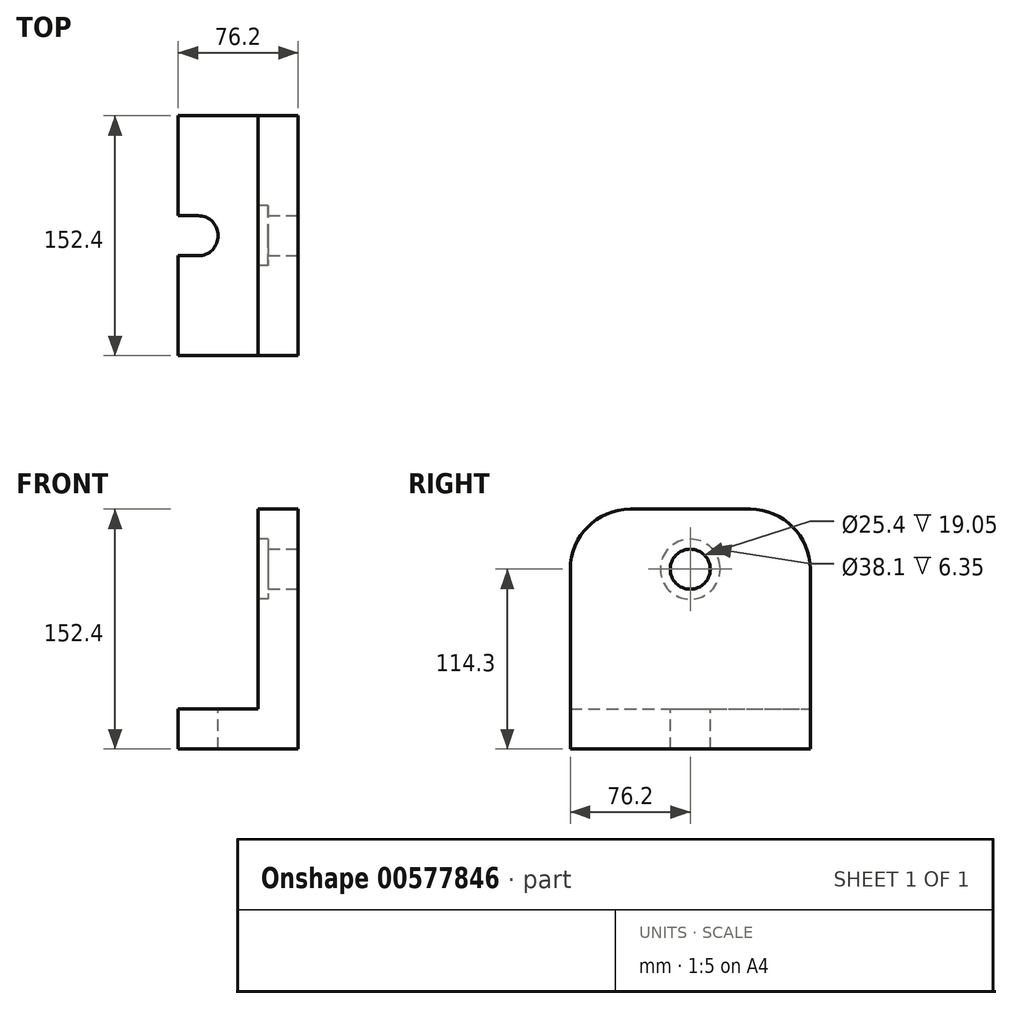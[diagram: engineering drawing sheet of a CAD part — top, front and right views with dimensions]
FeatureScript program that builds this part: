
annotation { "Feature Type Name" : "Feature", "Feature Type Description" : "" }
export const myFeature = defineFeature(function(context is Context, id is Id, definition is map)
    precondition{}
    {
        {
            var Q0;
            Q0=qCreatedBy(makeId("Front.planeOp"),FACE);
            var sketch = newSketch(context, id + "F0", { "sketchPlane" : qUnion([Q0])});
            skLineSegment(sketch, "E0.bottom", {"start": v(0, 0) * mm, "end": v(-76.2, 0) * mm});
            skLineSegment(sketch, "E0.top", {"start": v(-25.4, 25.4) * mm, "end": v(-76.2, 25.4) * mm});
            skLineSegment(sketch, "E0.left", {"start": v(0, 0) * mm, "end": v(0, 25.4) * mm});
            skLineSegment(sketch, "E0.right", {"start": v(-76.2, 0) * mm, "end": v(-76.2, 25.4) * mm});
            skLineSegment(sketch, "E1.bottom", {"start": v(0, 0) * mm, "end": v(-25.4, 0) * mm});
            skLineSegment(sketch, "E1.top", {"start": v(0, 152.4) * mm, "end": v(-25.4, 152.4) * mm});
            skLineSegment(sketch, "E1.left", {"start": v(0, 0) * mm, "end": v(0, 152.4) * mm});
            skLineSegment(sketch, "E1.right", {"start": v(-25.4, 25.4) * mm, "end": v(-25.4, 152.4) * mm});
            skSolve(sketch);
        }
        {
            var Q0;
            Q0=makeQuery(id+"F0.imprint","IMPRINT",FACE,{"disambiguationData":[TD([[makeQuery(id+"F0.imprint","IMPRINT",EDGE,{"derivedFrom":sQuery(id+"F0.wireOp",EDGE,"E0.bottom")}),-1.0]])]});
            extrude(context, id + "F1", {"entities" : qUnion([Q0]), "endBound" : BoundingType.SYMMETRIC, "depth" : 152.4 * mm, "offsetDistance" : 25.4 * mm});
        }
        {
            var Q0;
            Q0=makeQuery(id+"F1.opExtrude","SWEPT_FACE",FACE,{"disambiguationData":[OSD([sQuery(id+"F0.wireOp",EDGE,"E1.left")])]});
            var sketch = newSketch(context, id + "F2", { "sketchPlane" : qUnion([Q0])});
            skCircle(sketch, "E2", {"center": v(0, 114.3) * mm, "radius": 12.7 * mm});
            skSolve(sketch);
        }
        {
            var Q0;
            Q0=makeQuery(id+"F2.imprint","IMPRINT",FACE,{"disambiguationData":[TD([[makeQuery(id+"F2.imprint","IMPRINT",EDGE,{"derivedFrom":sQuery(id+"F2.wireOp",EDGE,"E2")}),1.0]])]});
            extrude(context, id + "F3", {"entities" : qUnion([Q0]), "operationType" : NewBodyOperationType.REMOVE, "endBound" : BoundingType.THROUGH_ALL, "oppositeDirection" : true, "depth" : 25.4 * mm, "offsetDistance" : 25.4 * mm});
        }
        {
            var Q0;
            Q0=makeQuery(id+"F1.opExtrude","SWEPT_FACE",FACE,{"disambiguationData":[OSD([sQuery(id+"F0.wireOp",EDGE,"E0.top")])]});
            var sketch = newSketch(context, id + "F4", { "sketchPlane" : qUnion([Q0])});
            skArc(sketch, "E3", {"start": v(-63.5, -12.7) * mm, "mid": v(-50.8, 0) * mm, "end": v(-63.5, 12.7) * mm});
            skLineSegment(sketch, "E4", {"start": v(-63.5, 12.7) * mm, "end": v(-76.2, 12.7) * mm});
            skLineSegment(sketch, "E5", {"start": v(-63.5, -12.7) * mm, "end": v(-76.2, -12.7) * mm});
            skPoint(sketch, "E6", {"position": v(-63.5, 12.7) * mm});
            skPoint(sketch, "E7", {"position": v(-63.5, -12.7) * mm});
            skSolve(sketch);
        }
        {
            var Q0;
            Q0=makeQuery(id+"F4.imprint","IMPRINT",FACE,{"disambiguationData":[TD([[makeQuery(id+"F4.imprint","IMPRINT",EDGE,{"derivedFrom":sQuery(id+"F4.wireOp",EDGE,"E3")}),1.0]])]});
            extrude(context, id + "F5", {"entities" : qUnion([Q0]), "operationType" : NewBodyOperationType.REMOVE, "oppositeDirection" : true, "depth" : 25.4 * mm, "offsetDistance" : 25.4 * mm});
        }
        {
            var Q0;
            Q0=makeQuery(id+"F1.opExtrude","CAP_EDGE",EDGE,{"disambiguationData":[OSD([sQuery(id+"F0.wireOp",EDGE,"E1.top")])],"isStart":false});
            var Q1;
            Q1=makeQuery(id+"F1.opExtrude","CAP_EDGE",EDGE,{"disambiguationData":[OSD([sQuery(id+"F0.wireOp",EDGE,"E1.top")])],"isStart":true});
            fillet(context, id + "F6", {"entities" : qUnion([Q0, Q1]), "radius" : 38.1 * mm, "tangentPropagation" : true, "allowEdgeOverflow" : false});
        }
        {
            var Q0;
            Q0=makeQuery(id+"F1.opExtrude","SWEPT_FACE",FACE,{"disambiguationData":[OSD([sQuery(id+"F0.wireOp",EDGE,"E1.right")])]});
            var sketch = newSketch(context, id + "F7", { "sketchPlane" : qUnion([Q0])});
            skPoint(sketch, "E8.first.point.positionSnap0", {"position": v(0, 25.4) * mm});
            skCircle(sketch, "E9", {"center": v(0, 114.3) * mm, "radius": 19.05 * mm});
            skSolve(sketch);
        }
        {
            var Q0;
            Q0=makeQuery(id+"F7.imprint","IMPRINT",FACE,{"disambiguationData":[TD([[makeQuery(id+"F7.imprint","IMPRINT",EDGE,{"derivedFrom":sQuery(id+"F7.wireOp",EDGE,"E9")}),1.0]])]});
            extrude(context, id + "F8", {"entities" : qUnion([Q0]), "operationType" : NewBodyOperationType.REMOVE, "oppositeDirection" : true, "depth" : 6.35 * mm, "offsetDistance" : 25.4 * mm});
        }
        {
            var Q0;
            Q0=qCreatedBy(makeId("Front.planeOp"),FACE);
            cPlane(context, id + "F9", {"entities" : qUnion([Q0]), "cplaneType" : CPlaneType.OFFSET, "offset" : 44.45 * mm, "width" : 152.4 * mm, "height" : 152.4 * mm});
        }
    });
